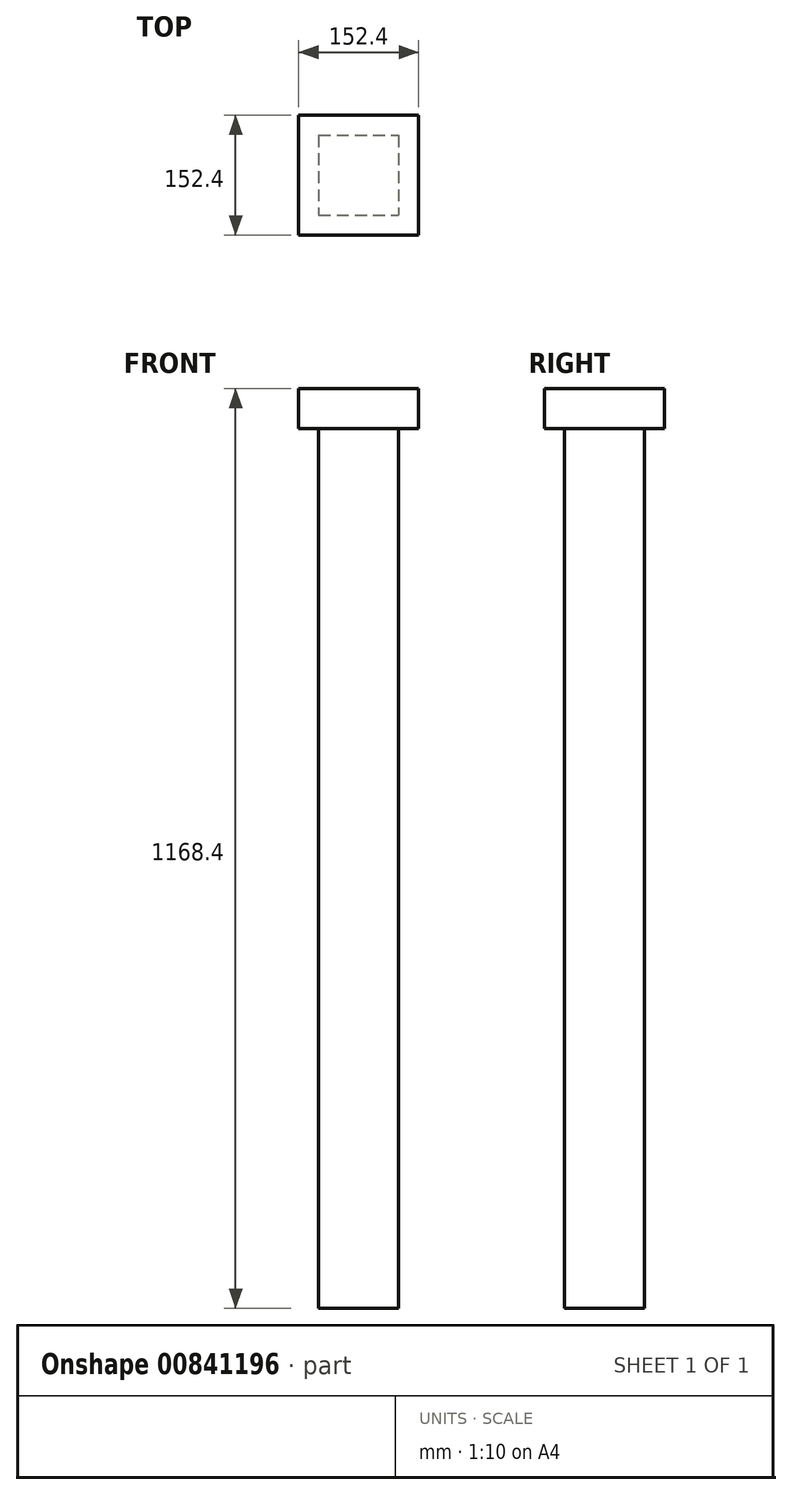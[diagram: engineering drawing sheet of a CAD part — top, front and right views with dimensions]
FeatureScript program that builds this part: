
annotation { "Feature Type Name" : "Feature", "Feature Type Description" : "" }
export const myFeature = defineFeature(function(context is Context, id is Id, definition is map)
    precondition{}
    {
        {
            var Q0;
            Q0=qCreatedBy(makeId("Top.planeOp"),FACE);
            var sketch = newSketch(context, id + "F0", { "sketchPlane" : qUnion([Q0])});
            skLineSegment(sketch, "E0.bottom", {"start": v(0, 0) * mm, "end": v(101.6, 0) * mm});
            skLineSegment(sketch, "E0.top", {"start": v(0, -101.6) * mm, "end": v(101.6, -101.6) * mm});
            skLineSegment(sketch, "E0.left", {"start": v(0, 0) * mm, "end": v(0, -101.6) * mm});
            skLineSegment(sketch, "E0.right", {"start": v(101.6, 0) * mm, "end": v(101.6, -101.6) * mm});
            skSolve(sketch);
        }
        {
            var Q0;
            Q0=makeQuery(id+"F0.imprint","IMPRINT",FACE,{"disambiguationData":[TD([[makeQuery(id+"F0.imprint","IMPRINT",EDGE,{"derivedFrom":sQuery(id+"F0.wireOp",EDGE,"E0.bottom")}),-1.0]])]});
            extrude(context, id + "F1", {"entities" : qUnion([Q0]), "oppositeDirection" : true, "depth" : 1117.6 * mm, "offsetDistance" : 25.4 * mm});
        }
        {
            var Q0;
            Q0=makeQuery(id+"F1.opExtrude","CAP_FACE",FACE,{"disambiguationData":[OSD([sQuery(id+"F0.wireOp",EDGE,"E0.bottom"),sQuery(id+"F0.wireOp",EDGE,"E0.top"),sQuery(id+"F0.wireOp",EDGE,"E0.left"),sQuery(id+"F0.wireOp",EDGE,"E0.right")])],"isStart":true});
            var sketch = newSketch(context, id + "F2", { "sketchPlane" : qUnion([Q0])});
            skLineSegment(sketch, "E1.bottom", {"start": v(-25.4, 25.4) * mm, "end": v(127, 25.4) * mm});
            skLineSegment(sketch, "E1.top", {"start": v(-25.4, -127) * mm, "end": v(127, -127) * mm});
            skLineSegment(sketch, "E1.left", {"start": v(-25.4, 25.4) * mm, "end": v(-25.4, -127) * mm});
            skLineSegment(sketch, "E1.right", {"start": v(127, 25.4) * mm, "end": v(127, -127) * mm});
            skSolve(sketch);
        }
        {
            var Q0;
            Q0 = qSketchRegion(id + "F2", true);
            extrude(context, id + "F3", {"entities" : qUnion([Q0]), "operationType" : NewBodyOperationType.ADD, "depth" : 50.8 * mm, "offsetDistance" : 25.4 * mm});
        }
    });
